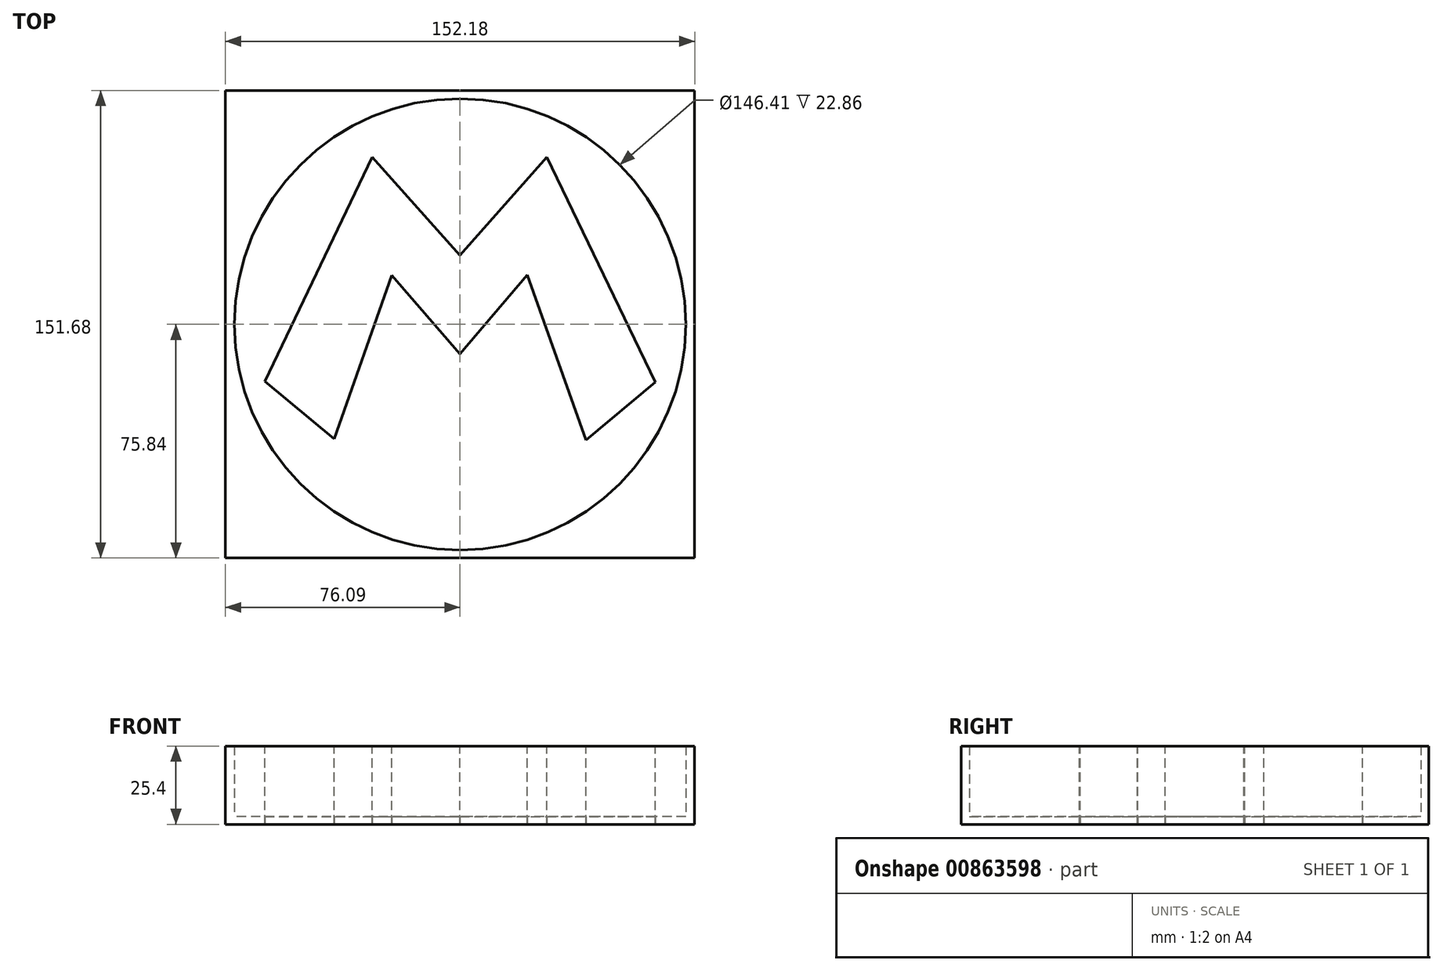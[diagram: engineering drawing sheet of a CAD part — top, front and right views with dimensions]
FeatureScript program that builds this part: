
annotation { "Feature Type Name" : "Feature", "Feature Type Description" : "" }
export const myFeature = defineFeature(function(context is Context, id is Id, definition is map)
    precondition{}
    {
        {
            var Q0;
            Q0=qCreatedBy(makeId("Top.planeOp"),FACE);
            var sketch = newSketch(context, id + "F0", { "sketchPlane" : qUnion([Q0])});
            skCircle(sketch, "E0", {"center": v(0, 0) * mm, "radius": 73.2 * mm});
            skLineSegment(sketch, "E1", {"start": v(-63.27, -18.53) * mm, "end": v(-28.52, 54.28) * mm});
            skLineSegment(sketch, "E2", {"start": v(-28.52, 54.28) * mm, "end": v(0, 22.32) * mm});
            skLineSegment(sketch, "E3", {"start": v(-63.27, -18.53) * mm, "end": v(-40.75, -37.23) * mm});
            skLineSegment(sketch, "E4", {"start": v(-40.75, -37.23) * mm, "end": v(-22.1, 15.84) * mm});
            skLineSegment(sketch, "E5", {"start": v(-22.1, 15.84) * mm, "end": v(0, -9.65) * mm});
            skLineSegment(sketch, "E6", {"start": v(0, 22.32) * mm, "end": v(28.15, 54.3) * mm});
            skLineSegment(sketch, "E7", {"start": v(28.15, 54.3) * mm, "end": v(63.31, -18.74) * mm});
            skLineSegment(sketch, "E8", {"start": v(63.31, -18.74) * mm, "end": v(40.84, -37.55) * mm});
            skLineSegment(sketch, "E9", {"start": v(40.84, -37.55) * mm, "end": v(21.79, 16.04) * mm});
            skLineSegment(sketch, "E10", {"start": v(21.79, 16.04) * mm, "end": v(0, -9.65) * mm});
            skLineSegment(sketch, "E11.bottom", {"start": v(76.09, -75.84) * mm, "end": v(-76.09, -75.84) * mm});
            skLineSegment(sketch, "E11.top", {"start": v(76.09, 75.84) * mm, "end": v(-76.09, 75.84) * mm});
            skLineSegment(sketch, "E11.left", {"start": v(76.09, -75.84) * mm, "end": v(76.09, 75.84) * mm});
            skLineSegment(sketch, "E11.right", {"start": v(-76.09, -75.84) * mm, "end": v(-76.09, 75.84) * mm});
            skSolve(sketch);
        }
        {
            var Q0;
            Q0=makeQuery(id+"F0.imprint","IMPRINT",FACE,{"disambiguationData":[TD([[makeQuery(id+"F0.imprint","IMPRINT",EDGE,{"derivedFrom":sQuery(id+"F0.wireOp",EDGE,"E0")}),1.0]])]});
            extrude(context, id + "F1", {"entities" : qUnion([Q0]), "depth" : 2.54 * mm, "offsetDistance" : 25.4 * mm});
        }
        {
            var Q0;
            Q0 = qSketchRegion(id + "F0", true);
            extrude(context, id + "F2", {"entities" : qUnion([Q0]), "operationType" : NewBodyOperationType.ADD, "depth" : 25.4 * mm, "offsetDistance" : 25.4 * mm});
        }
        {
            var Q0;
            Q0=makeQuery(id+"F2.opExtrude","CAP_FACE",FACE,{"disambiguationData":[OSD([sQuery(id+"F0.wireOp",EDGE,"E0"),sQuery(id+"F0.wireOp",EDGE,"E11.bottom"),sQuery(id+"F0.wireOp",EDGE,"E11.top"),sQuery(id+"F0.wireOp",EDGE,"E11.left"),sQuery(id+"F0.wireOp",EDGE,"E11.right")])],"isStart":false});
            var sketch = newSketch(context, id + "F3", { "sketchPlane" : qUnion([Q0])});
            skLineSegment(sketch, "E12.0", {"start": v(-63.27, -18.53) * mm, "end": v(-28.52, 54.28) * mm});
            skLineSegment(sketch, "E13.0", {"start": v(-28.52, 54.28) * mm, "end": v(0, 22.32) * mm});
            skLineSegment(sketch, "E14.0", {"start": v(0, 22.32) * mm, "end": v(28.15, 54.3) * mm});
            skLineSegment(sketch, "E15.0", {"start": v(28.15, 54.3) * mm, "end": v(63.31, -18.74) * mm});
            skLineSegment(sketch, "E16.0", {"start": v(63.31, -18.74) * mm, "end": v(40.84, -37.55) * mm});
            skLineSegment(sketch, "E17.0", {"start": v(40.84, -37.55) * mm, "end": v(21.79, 16.04) * mm});
            skLineSegment(sketch, "E18.0", {"start": v(21.79, 16.04) * mm, "end": v(0, -9.65) * mm});
            skLineSegment(sketch, "E19.0", {"start": v(-22.1, 15.84) * mm, "end": v(0, -9.65) * mm});
            skLineSegment(sketch, "E20.0", {"start": v(-40.75, -37.23) * mm, "end": v(-22.1, 15.84) * mm});
            skLineSegment(sketch, "E21.0", {"start": v(-63.27, -18.53) * mm, "end": v(-40.75, -37.23) * mm});
            skSolve(sketch);
        }
        {
            var Q0;
            Q0=makeQuery(id+"F3.imprint","IMPRINT",FACE,{"disambiguationData":[TD([[makeQuery(id+"F3.imprint","IMPRINT",EDGE,{"derivedFrom":sQuery(id+"F3.wireOp",EDGE,"E12.0")}),-1.0]])]});
            extrude(context, id + "F4", {"entities" : qUnion([Q0]), "oppositeDirection" : true, "depth" : 25.4 * mm, "offsetDistance" : 25.4 * mm});
        }
    });
